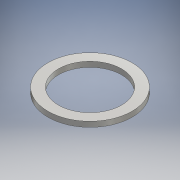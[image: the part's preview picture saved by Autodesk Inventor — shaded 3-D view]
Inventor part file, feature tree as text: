
AUTODESK INVENTOR PART (.ipt)
format: ipt  version: 2016 (Build 200138000, 138)  size: 97,792 bytes
history: native  units: mm
features: other x1, extrude x1, sketch x1
ambient origin geometry x8: Origin, YZ Plane, XZ Plane, XY Plane, X Axis, Y Axis, Z Axis, Center Point
bodies: Body1 (feature_tree)
feature tree (3):
  other  "ソリッド1"
  extrude  "押し出し1"  Depth=6.0mm
  sketch  "スケッチ1"
